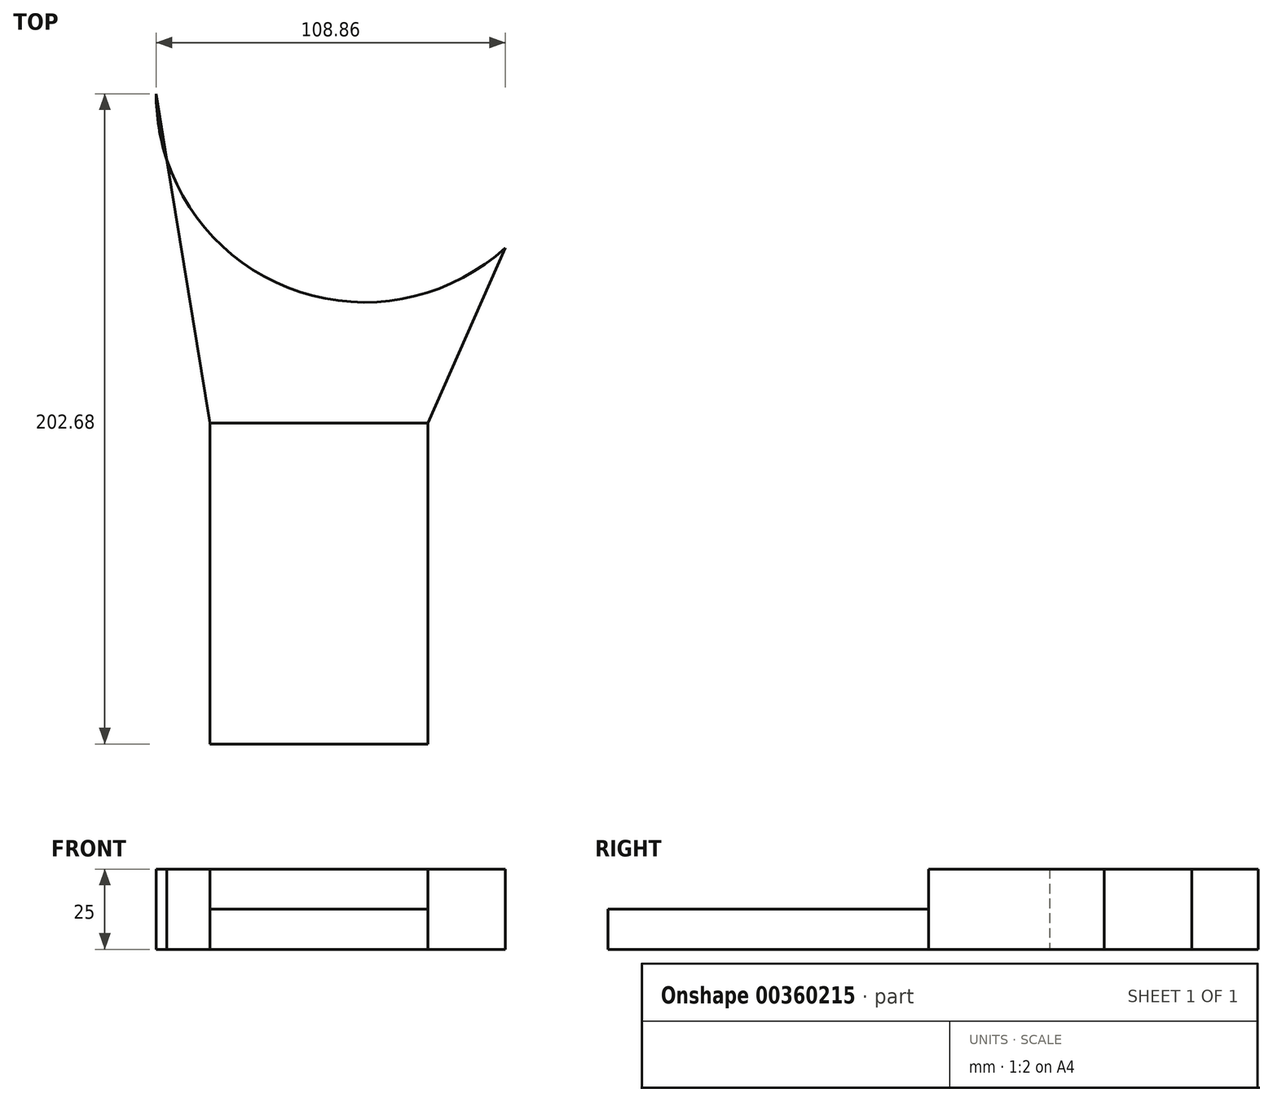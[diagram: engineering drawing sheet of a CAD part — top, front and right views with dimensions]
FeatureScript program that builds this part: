
annotation { "Feature Type Name" : "Feature", "Feature Type Description" : "" }
export const myFeature = defineFeature(function(context is Context, id is Id, definition is map)
    precondition{}
    {
        {
            var Q0;
            Q0=qCreatedBy(makeId("Top.planeOp"),FACE);
            var sketch = newSketch(context, id + "F0", { "sketchPlane" : qUnion([Q0])});
            skCircle(sketch, "E0", {"center": v(0, 0) * mm, "radius": 65 * mm});
            skLineSegment(sketch, "E1", {"start": v(-65, 0) * mm, "end": v(-48.25, -102.68) * mm});
            skLineSegment(sketch, "E2", {"start": v(-48.25, -102.68) * mm, "end": v(-48.25, -202.68) * mm});
            skLineSegment(sketch, "E3", {"start": v(-48.25, -202.68) * mm, "end": v(19.75, -202.68) * mm});
            skLineSegment(sketch, "E4", {"start": v(19.75, -202.68) * mm, "end": v(19.75, -102.68) * mm});
            skLineSegment(sketch, "E5", {"start": v(19.75, -102.68) * mm, "end": v(65, 0) * mm});
            skSolve(sketch);
        }
        {
            var Q0;
            {var subQ0=sQuery(id+"F0.wireOp",EDGE,"E1");var subQ1=sQuery(id+"F0.wireOp",EDGE,"E0");var subQ2=makeQuery(id+"F0.imprint","INTERSECT",VERTEX,{"disambiguationData":[OD(0.0)],"derivedFrom":[subQ1,subQ0]});Q0=makeQuery(id+"F0.imprint","IMPRINT",FACE,{"disambiguationData":[TD([[makeQuery(id+"F0.imprint","IMPRINT",EDGE,{"disambiguationData":[TD([[subQ2,1.0]])],"derivedFrom":subQ1}),1.0]])]});}
            var Q1;
            {var subQ0=sQuery(id+"F0.wireOp",EDGE,"E2");Q1=makeQuery(id+"F0.imprint","IMPRINT",FACE,{"disambiguationData":[TD([[makeQuery(id+"F0.imprint","IMPRINT",EDGE,{"derivedFrom":subQ0}),1.0]])]});}
            extrude(context, id + "F1", {"entities" : qUnion([Q0, Q1]), "depth" : 25 * mm});
        }
        {
            var Q0;
            Q0=makeQuery(id+"F1.opExtrude","CAP_FACE",FACE,{"disambiguationData":[OSD([sQuery(id+"F0.wireOp",EDGE,"E0"),sQuery(id+"F0.wireOp",EDGE,"E1"),sQuery(id+"F0.wireOp",EDGE,"E2"),sQuery(id+"F0.wireOp",EDGE,"E3"),sQuery(id+"F0.wireOp",EDGE,"E4"),sQuery(id+"F0.wireOp",EDGE,"E5")])],"isStart":true});
            var sketch = newSketch(context, id + "F2", { "sketchPlane" : qUnion([Q0])});
            skCircle(sketch, "E6", {"center": v(-8.12, 0) * mm, "radius": 43.26 * mm});
            skSolve(sketch);
        }
        {
            var Q0;
            Q0=makeQuery(id+"F2.imprint","IMPRINT",FACE,{"disambiguationData":[TD([[makeQuery(id+"F2.imprint","IMPRINT",EDGE,{"derivedFrom":sQuery(id+"F2.wireOp",EDGE,"E6")}),1.0]])]});
            extrude(context, id + "F3", {"entities" : qUnion([Q0]), "operationType" : NewBodyOperationType.REMOVE, "oppositeDirection" : true, "depth" : 20 * mm});
        }
        {
            var Q0;
            Q0=makeQuery(id+"F1.opExtrude","SWEPT_FACE",FACE,{"disambiguationData":[OSD([sQuery(id+"F0.wireOp",EDGE,"E2")])]});
            var sketch = newSketch(context, id + "F4", { "sketchPlane" : qUnion([Q0])});
            skLineSegment(sketch, "E7", {"start": v(202.68, 12.5) * mm, "end": v(102.68, 12.5) * mm});
            skLineSegment(sketch, "E8", {"start": v(102.68, 12.5) * mm, "end": v(102.68, 25) * mm});
            skLineSegment(sketch, "E9", {"start": v(102.68, 25) * mm, "end": v(202.68, 25) * mm});
            skLineSegment(sketch, "E10", {"start": v(202.68, 25) * mm, "end": v(202.68, 12.5) * mm});
            skSolve(sketch);
        }
        {
            var Q0;
            Q0 = qSketchRegion(id + "F4", true);
            extrude(context, id + "F5", {"entities" : qUnion([Q0]), "operationType" : NewBodyOperationType.REMOVE, "endBound" : BoundingType.THROUGH_ALL, "oppositeDirection" : true, "depth" : 25.4 * mm});
        }
    });
